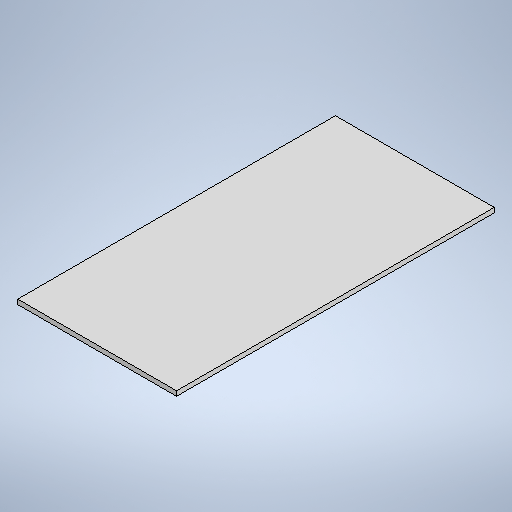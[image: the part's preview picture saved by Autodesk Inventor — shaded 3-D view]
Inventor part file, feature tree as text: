
AUTODESK INVENTOR PART (.ipt)
format: ipt  version: 2025 (Build 290162010, 162A)  size: 227,328 bytes
history: native  units: mm
features: sheet_metal_op x1, sketch x1, other x1
ambient origin geometry x8: Origin, YZ Plane, XZ Plane, XY Plane, X Axis, Y Axis, Z Axis, Center Point
bodies: Solid1 (feature_tree)
feature tree (3):
  sheet_metal_op  "Face1"
  sketch  "Sketch1"  dims[d0=100.0mm d1=200.0mm d2=3.0mm]
  other  "Plate1"
